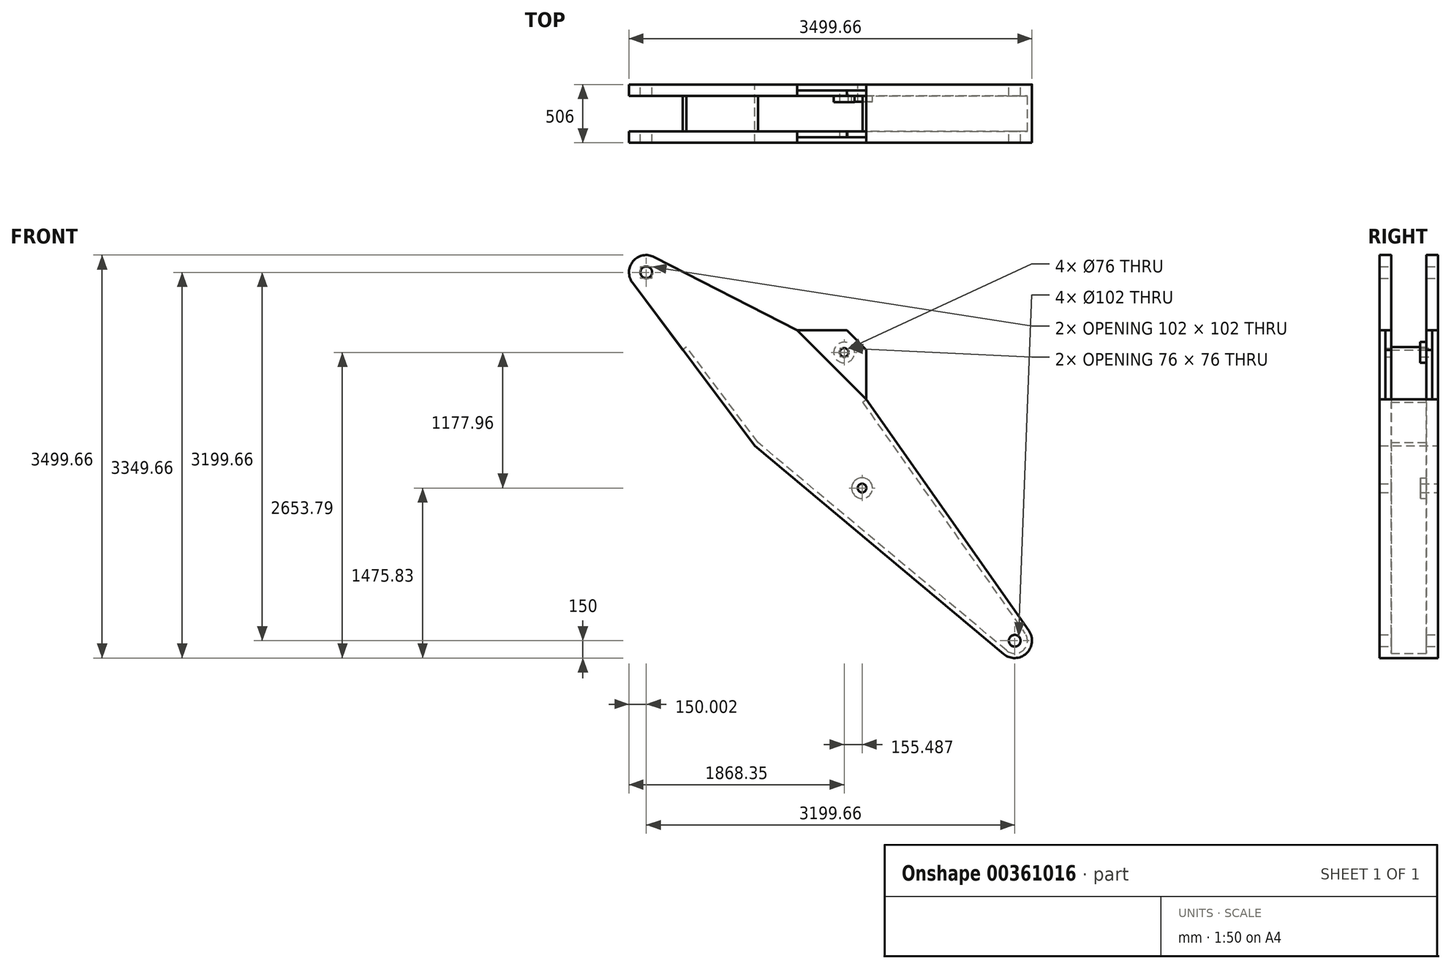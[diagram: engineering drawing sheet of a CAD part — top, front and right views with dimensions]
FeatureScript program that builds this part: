
annotation { "Feature Type Name" : "Feature", "Feature Type Description" : "" }
export const myFeature = defineFeature(function(context is Context, id is Id, definition is map)
    precondition{}
    {
        {
            var Q0;
            Q0=qCreatedBy(makeId("Front.planeOp"),FACE);
            var sketch = newSketch(context, id + "F0", { "sketchPlane" : qUnion([Q0])});
            skLineSegment(sketch, "E0", {"start": v(-1730, 0) * mm, "end": v(2795, 0) * mm, "construction": true});
            skCircle(sketch, "E1", {"center": v(-1730, 0) * mm, "radius": 51 * mm});
            skCircle(sketch, "E2", {"center": v(2795, 0) * mm, "radius": 51 * mm});
            skArc(sketch, "E3", {"start": v(-1775.92, 142.8) * mm, "mid": v(-1879.47, -12.62) * mm, "end": v(-1751.32, -148.48) * mm});
            skArc(sketch, "E4", {"start": v(2820.8, 147.77) * mm, "mid": v(2944.87, -6.28) * mm, "end": v(2808.33, -149.4) * mm});
            skLineSegment(sketch, "E5", {"start": v(-1751.32, -148.48) * mm, "end": v(0, -400) * mm});
            skLineSegment(sketch, "E6", {"start": v(-1775.92, 142.8) * mm, "end": v(-447.5, 570) * mm});
            skLineSegment(sketch, "E7", {"start": v(0, -400) * mm, "end": v(2808.33, -149.4) * mm});
            skLineSegment(sketch, "E8", {"start": v(2820.8, 147.77) * mm, "end": v(401.72, 570) * mm});
            skLineSegment(sketch, "E9", {"start": v(-447.5, 570) * mm, "end": v(-142.5, 875) * mm});
            skLineSegment(sketch, "E10", {"start": v(-142.5, 875) * mm, "end": v(96.72, 875) * mm});
            skLineSegment(sketch, "E11", {"start": v(96.72, 875) * mm, "end": v(401.72, 570) * mm});
            skLineSegment(sketch, "E12", {"start": v(-447.5, 570) * mm, "end": v(401.72, 570) * mm, "construction": true});
            skCircle(sketch, "E13", {"center": v(-22.9, 723) * mm, "radius": 38 * mm});
            skPoint(sketch, "E13.centerSnap0", {"position": v(-22.9, 875) * mm});
            skCircle(sketch, "E14", {"center": v(920, 0) * mm, "radius": 38 * mm});
            skSolve(sketch);
        }
        {
            var Q0;
            Q0=makeQuery(id+"F0.imprint","IMPRINT",FACE,{"disambiguationData":[TD([[makeQuery(id+"F0.imprint","IMPRINT",EDGE,{"derivedFrom":sQuery(id+"F0.wireOp",EDGE,"E1")}),-1.0]])]});
            extrude(context, id + "F1", {"entities" : qUnion([Q0]), "endBound" : BoundingType.SYMMETRIC, "depth" : 506 * mm});
        }
        {
            var Q0;
            Q0=makeQuery(id+"F1.opExtrude","SWEPT_FACE",FACE,{"disambiguationData":[OSD([sQuery(id+"F0.wireOp",EDGE,"E10")])]});
            var sketch = newSketch(context, id + "F2", { "sketchPlane" : qUnion([Q0])});
            skLineSegment(sketch, "E15.bottom", {"start": v(3116.88, 153) * mm, "end": v(-3116.88, 153) * mm});
            skLineSegment(sketch, "E15.top", {"start": v(3116.88, -153) * mm, "end": v(-3116.88, -153) * mm});
            skLineSegment(sketch, "E15.left", {"start": v(3116.88, 153) * mm, "end": v(3116.88, -153) * mm});
            skLineSegment(sketch, "E15.right", {"start": v(-3116.88, 153) * mm, "end": v(-3116.88, -153) * mm});
            skPoint(sketch, "E15.middle", {"position": v(0, 0) * mm});
            skSolve(sketch);
        }
        {
            var Q0;
            Q0 = qSketchRegion(id + "F2", true);
            extrude(context, id + "F3", {"entities" : qUnion([Q0]), "operationType" : NewBodyOperationType.REMOVE, "endBound" : BoundingType.THROUGH_ALL, "oppositeDirection" : true, "depth" : 25 * mm});
        }
        {
            var Q0;
            Q0=makeQuery(id+"F3.boolean.opBoolean","COPY",FACE,{"derivedFrom":makeQuery(id+"F3.opExtrude","SWEPT_FACE",FACE,{"disambiguationData":[OSD([sQuery(id+"F2.wireOp",EDGE,"E15.bottom")])]})});
            var sketch = newSketch(context, id + "F4", { "sketchPlane" : qUnion([Q0])});
            skCircle(sketch, "E16", {"center": v(-22.9, 723) * mm, "radius": 90 * mm});
            skSolve(sketch);
        }
        {
            var Q0;
            Q0=makeQuery(id+"F4.imprint","IMPRINT",FACE,{"disambiguationData":[TD([[makeQuery(id+"F4.imprint","IMPRINT",EDGE,{"derivedFrom":sQuery(id+"F4.wireOp",EDGE,"E16")}),1.0]])]});
            extrude(context, id + "F5", {"entities" : qUnion([Q0]), "operationType" : NewBodyOperationType.ADD, "depth" : 53 * mm});
        }
        {
            var Q0;
            Q0=makeQuery(id+"F1.opExtrude","CAP_FACE",FACE,{"disambiguationData":[OSD([sQuery(id+"F0.wireOp",EDGE,"E1"),sQuery(id+"F0.wireOp",EDGE,"E2"),sQuery(id+"F0.wireOp",EDGE,"E3"),sQuery(id+"F0.wireOp",EDGE,"E4"),sQuery(id+"F0.wireOp",EDGE,"E5"),sQuery(id+"F0.wireOp",EDGE,"E6"),sQuery(id+"F0.wireOp",EDGE,"E7"),sQuery(id+"F0.wireOp",EDGE,"E8"),sQuery(id+"F0.wireOp",EDGE,"E9"),sQuery(id+"F0.wireOp",EDGE,"E10"),sQuery(id+"F0.wireOp",EDGE,"E11"),sQuery(id+"F0.wireOp",EDGE,"E13"),sQuery(id+"F0.wireOp",EDGE,"E14")])],"isStart":false});
            var sketch = newSketch(context, id + "F6", { "sketchPlane" : qUnion([Q0])});
            skLineSegment(sketch, "E17.0", {"start": v(-447.5, 570) * mm, "end": v(-142.5, 875) * mm});
            skLineSegment(sketch, "E18.0", {"start": v(-142.5, 875) * mm, "end": v(96.72, 875) * mm});
            skLineSegment(sketch, "E19.0", {"start": v(96.72, 875) * mm, "end": v(401.72, 570) * mm});
            skLineSegment(sketch, "E20", {"start": v(-447.5, 570) * mm, "end": v(401.72, 570) * mm});
            skSolve(sketch);
        }
        {
            var Q0;
            Q0=makeQuery(id+"F6.imprint","IMPRINT",FACE,{"disambiguationData":[TD([[makeQuery(id+"F6.imprint","IMPRINT",EDGE,{"derivedFrom":sQuery(id+"F6.wireOp",EDGE,"E17.0")}),-1.0]])]});
            extrude(context, id + "F7", {"entities" : qUnion([Q0]), "operationType" : NewBodyOperationType.REMOVE, "oppositeDirection" : true, "depth" : 50 * mm});
        }
        {
            var Q0;
            Q0=makeQuery(id+"F1.opExtrude","CAP_FACE",FACE,{"disambiguationData":[OSD([sQuery(id+"F0.wireOp",EDGE,"E1"),sQuery(id+"F0.wireOp",EDGE,"E2"),sQuery(id+"F0.wireOp",EDGE,"E3"),sQuery(id+"F0.wireOp",EDGE,"E4"),sQuery(id+"F0.wireOp",EDGE,"E5"),sQuery(id+"F0.wireOp",EDGE,"E6"),sQuery(id+"F0.wireOp",EDGE,"E7"),sQuery(id+"F0.wireOp",EDGE,"E8"),sQuery(id+"F0.wireOp",EDGE,"E9"),sQuery(id+"F0.wireOp",EDGE,"E10"),sQuery(id+"F0.wireOp",EDGE,"E11"),sQuery(id+"F0.wireOp",EDGE,"E13"),sQuery(id+"F0.wireOp",EDGE,"E14")])],"isStart":true});
            var sketch = newSketch(context, id + "F8", { "sketchPlane" : qUnion([Q0])});
            skLineSegment(sketch, "E21.0", {"start": v(-96.72, 875) * mm, "end": v(-401.72, 570) * mm});
            skLineSegment(sketch, "E22.0", {"start": v(142.5, 875) * mm, "end": v(-96.72, 875) * mm});
            skLineSegment(sketch, "E23.0", {"start": v(447.5, 570) * mm, "end": v(142.5, 875) * mm});
            skLineSegment(sketch, "E24", {"start": v(-401.72, 570) * mm, "end": v(447.5, 570) * mm});
            skSolve(sketch);
        }
        {
            var Q0;
            Q0=makeQuery(id+"F8.imprint","IMPRINT",FACE,{"disambiguationData":[TD([[makeQuery(id+"F8.imprint","IMPRINT",EDGE,{"derivedFrom":sQuery(id+"F8.wireOp",EDGE,"E21.0")}),1.0]])]});
            extrude(context, id + "F9", {"entities" : qUnion([Q0]), "operationType" : NewBodyOperationType.REMOVE, "oppositeDirection" : true, "depth" : 50 * mm});
        }
        {
            var Q0;
            Q0=makeQuery(id+"F3.boolean.opBoolean","COPY",FACE,{"derivedFrom":makeQuery(id+"F3.opExtrude","SWEPT_FACE",FACE,{"disambiguationData":[OSD([sQuery(id+"F2.wireOp",EDGE,"E15.bottom")])]})});
            var sketch = newSketch(context, id + "F10", { "sketchPlane" : qUnion([Q0])});
            skCircle(sketch, "E25", {"center": v(920, 0) * mm, "radius": 90 * mm});
            skSolve(sketch);
        }
        {
            var Q0;
            Q0=makeQuery(id+"F10.imprint","IMPRINT",FACE,{"disambiguationData":[TD([[makeQuery(id+"F10.imprint","IMPRINT",EDGE,{"derivedFrom":sQuery(id+"F10.wireOp",EDGE,"E25")}),1.0]])]});
            extrude(context, id + "F11", {"entities" : qUnion([Q0]), "operationType" : NewBodyOperationType.ADD, "depth" : 50 * mm});
        }
        {
            var Q0;
            Q0=makeQuery(id+"F3.boolean.opBoolean","COPY",FACE,{"derivedFrom":makeQuery(id+"F3.opExtrude","SWEPT_FACE",FACE,{"disambiguationData":[OSD([sQuery(id+"F2.wireOp",EDGE,"E15.bottom")])]})});
            var sketch = newSketch(context, id + "F12", { "sketchPlane" : qUnion([Q0])});
            skLineSegment(sketch, "E26.0", {"start": v(394.84, 530.6) * mm, "end": v(2813.91, 108.36) * mm});
            skArc(sketch, "E27.0", {"start": v(2804.78, -109.56) * mm, "mid": v(2904.9, -4.6) * mm, "end": v(2813.91, 108.36) * mm});
            skLineSegment(sketch, "E28.0", {"start": v(2804.78, -109.56) * mm, "end": v(1.08, -359.74) * mm});
            skLineSegment(sketch, "E29.0", {"start": v(1.08, -359.74) * mm, "end": v(-1024, -212.52) * mm});
            skLineSegment(sketch, "E30", {"start": v(394.84, 530.6) * mm, "end": v(401.72, 570) * mm});
            skCircle(sketch, "E31.0", {"center": v(-1730, 0) * mm, "radius": 51 * mm});
            skLineSegment(sketch, "E32", {"start": v(-1024, -212.52) * mm, "end": v(-1029.69, -252.12) * mm});
            skSolve(sketch);
        }
        {
            var Q0;
            Q0=makeQuery(id+"F12.imprint","IMPRINT",FACE,{"disambiguationData":[TD([[makeQuery(id+"F12.imprint","IMPRINT",EDGE,{"derivedFrom":sQuery(id+"F12.wireOp",EDGE,"E26.0")}),1.0]])]});
            var Q1;
            Q1=makeQuery(id+"F3.boolean.opBoolean","COPY",FACE,{"derivedFrom":makeQuery(id+"F3.opExtrude","SWEPT_FACE",FACE,{"disambiguationData":[OSD([sQuery(id+"F2.wireOp",EDGE,"E15.top")])]})});
            extrude(context, id + "F13", {"entities" : qUnion([Q0]), "endBound" : BoundingType.UP_TO_SURFACE, "endBoundEntityFace" : qUnion([Q1]), "depth" : 25 * mm});
        }
        {
            var Q0;
            Q0=makeQuery(id+"F3.boolean.opBoolean","SPLIT",BODY,{"disambiguationData":[OD(0.0)],"derivedFrom":makeQuery(id+"F1.opExtrude","SWEPT_BODY",BODY,{"disambiguationData":[OSD([sQuery(id+"F0.wireOp",EDGE,"E1"),sQuery(id+"F0.wireOp",EDGE,"E2"),sQuery(id+"F0.wireOp",EDGE,"E3"),sQuery(id+"F0.wireOp",EDGE,"E4"),sQuery(id+"F0.wireOp",EDGE,"E5"),sQuery(id+"F0.wireOp",EDGE,"E6"),sQuery(id+"F0.wireOp",EDGE,"E7"),sQuery(id+"F0.wireOp",EDGE,"E8"),sQuery(id+"F0.wireOp",EDGE,"E9"),sQuery(id+"F0.wireOp",EDGE,"E10"),sQuery(id+"F0.wireOp",EDGE,"E11"),sQuery(id+"F0.wireOp",EDGE,"E13"),sQuery(id+"F0.wireOp",EDGE,"E14")])]})});
            var Q1;
            Q1=makeQuery(id+"F3.boolean.opBoolean","SPLIT",BODY,{"disambiguationData":[OD(1.0)],"derivedFrom":makeQuery(id+"F1.opExtrude","SWEPT_BODY",BODY,{"disambiguationData":[OSD([sQuery(id+"F0.wireOp",EDGE,"E1"),sQuery(id+"F0.wireOp",EDGE,"E2"),sQuery(id+"F0.wireOp",EDGE,"E3"),sQuery(id+"F0.wireOp",EDGE,"E4"),sQuery(id+"F0.wireOp",EDGE,"E5"),sQuery(id+"F0.wireOp",EDGE,"E6"),sQuery(id+"F0.wireOp",EDGE,"E7"),sQuery(id+"F0.wireOp",EDGE,"E8"),sQuery(id+"F0.wireOp",EDGE,"E9"),sQuery(id+"F0.wireOp",EDGE,"E10"),sQuery(id+"F0.wireOp",EDGE,"E11"),sQuery(id+"F0.wireOp",EDGE,"E13"),sQuery(id+"F0.wireOp",EDGE,"E14")])]})});
            var Q2;
            Q2=makeQuery(id+"F13.opExtrude","SWEPT_BODY",BODY,{"disambiguationData":[OSD([sQuery(id+"F0.wireOp",EDGE,"E4"),sQuery(id+"F0.wireOp",EDGE,"E5"),sQuery(id+"F0.wireOp",EDGE,"E7"),sQuery(id+"F0.wireOp",EDGE,"E8"),sQuery(id+"F2.wireOp",EDGE,"E15.bottom"),sQuery(id+"F12.wireOp",EDGE,"E26.0"),sQuery(id+"F12.wireOp",EDGE,"E27.0"),sQuery(id+"F12.wireOp",EDGE,"E28.0"),sQuery(id+"F12.wireOp",EDGE,"E29.0"),sQuery(id+"F12.wireOp",EDGE,"E30"),sQuery(id+"F12.wireOp",EDGE,"E32")])]});
            booleanBodies(context, id + "F14", {"operationType" : BooleanOperationType.UNION, "tools" : qUnion([Q0, Q1, Q2])});
        }
        {
            var Q0;
            Q0=makeQuery(id+"F3.boolean.opBoolean","SPLIT",BODY,{"disambiguationData":[OD(0.0)],"derivedFrom":makeQuery(id+"F1.opExtrude","SWEPT_BODY",BODY,{"disambiguationData":[OSD([sQuery(id+"F0.wireOp",EDGE,"E1"),sQuery(id+"F0.wireOp",EDGE,"E2"),sQuery(id+"F0.wireOp",EDGE,"E3"),sQuery(id+"F0.wireOp",EDGE,"E4"),sQuery(id+"F0.wireOp",EDGE,"E5"),sQuery(id+"F0.wireOp",EDGE,"E6"),sQuery(id+"F0.wireOp",EDGE,"E7"),sQuery(id+"F0.wireOp",EDGE,"E8"),sQuery(id+"F0.wireOp",EDGE,"E9"),sQuery(id+"F0.wireOp",EDGE,"E10"),sQuery(id+"F0.wireOp",EDGE,"E11"),sQuery(id+"F0.wireOp",EDGE,"E13"),sQuery(id+"F0.wireOp",EDGE,"E14")])]})});
            var Q1;
            {var subQ0=sQuery(id+"F2.wireOp",EDGE,"E15.bottom");var subQ1=sQuery(id+"F0.wireOp",EDGE,"E4");var subQ16=makeQuery(id+"F1.opExtrude","SWEPT_FACE",FACE,{"disambiguationData":[OSD([subQ1])]});Q1=makeQuery(id+"F14.opBoolean","MERGE",FACE,{"derivedFrom":[makeQuery(id+"F3.boolean.opBoolean","SPLIT",FACE,{"disambiguationData":[TD([makeQuery(id+"F3.opExtrude","SWEPT_FACE",FACE,{"disambiguationData":[OSD([subQ0])]})])],"derivedFrom":subQ16}),makeQuery(id+"F3.boolean.opBoolean","SPLIT",FACE,{"disambiguationData":[TD([makeQuery(id+"F3.opExtrude","SWEPT_FACE",FACE,{"disambiguationData":[OSD([sQuery(id+"F2.wireOp",EDGE,"E15.top")])]})])],"derivedFrom":subQ16}),makeQuery(id+"F13.opExtrude","SWEPT_FACE",FACE,{"disambiguationData":[OSD([subQ1,subQ0])]})]});}
            transform(context, id + "F15", {"entities" : qUnion([Q0]), "transformType" : TransformType.ROTATION, "transformAxis" : qUnion([Q1]), "angle" : 45 * degree, "makeCopy" : false});
        }
    });
